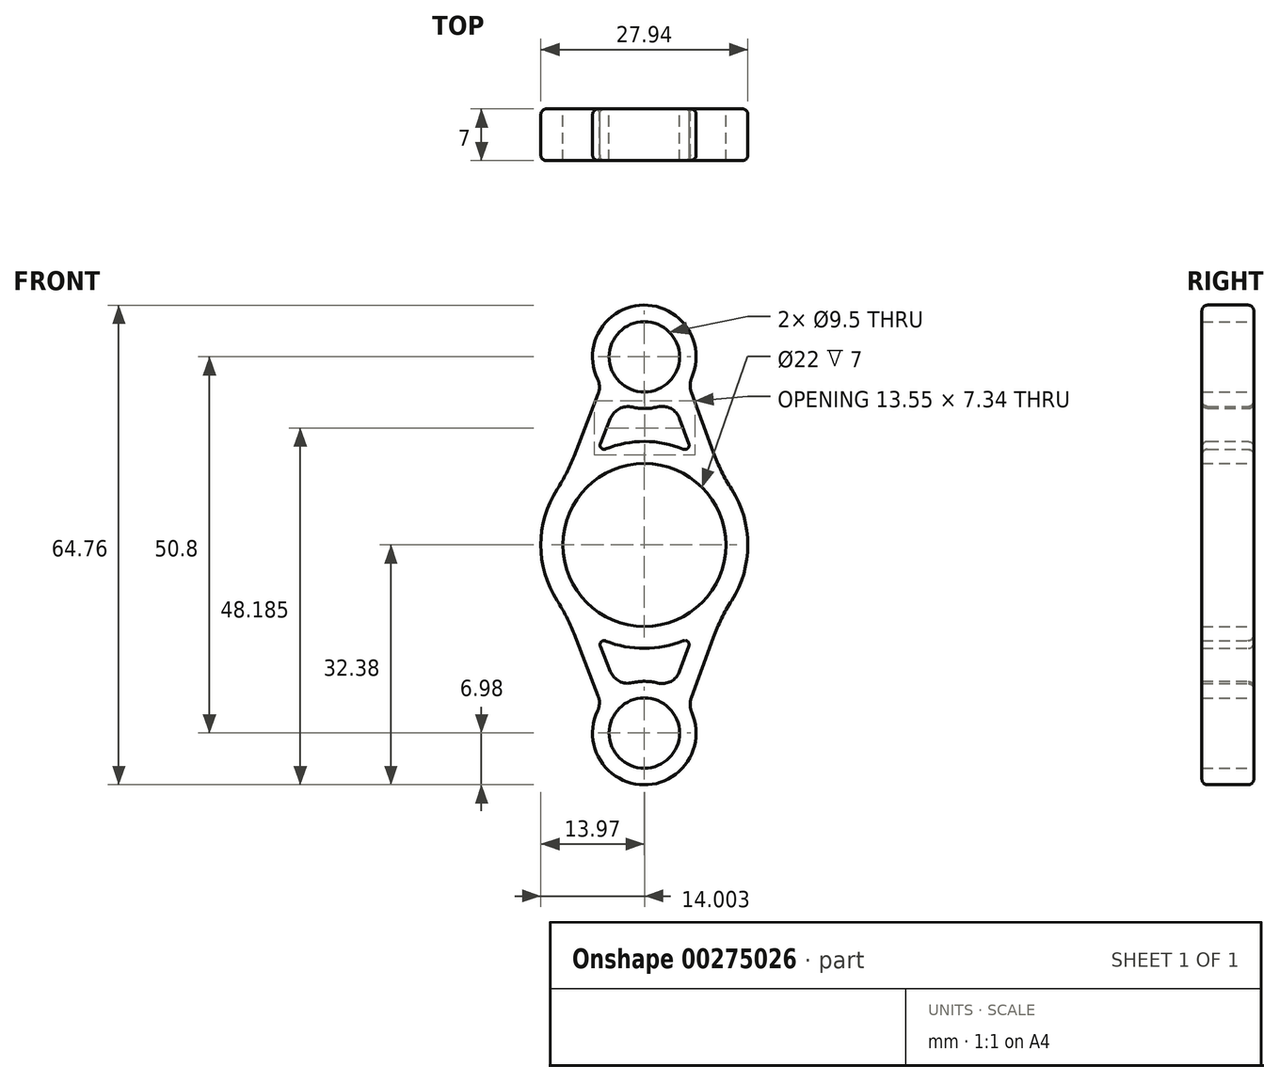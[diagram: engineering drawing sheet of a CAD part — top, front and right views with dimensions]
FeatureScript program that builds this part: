
annotation { "Feature Type Name" : "Feature", "Feature Type Description" : "" }
export const myFeature = defineFeature(function(context is Context, id is Id, definition is map)
    precondition{}
    {
        {
            var Q0;
            Q0=qCreatedBy(makeId("Front.planeOp"),FACE);
            var sketch = newSketch(context, id + "F0", { "sketchPlane" : qUnion([Q0])});
            skCircle(sketch, "E0", {"center": v(0, 0) * mm, "radius": 11 * mm});
            skArc(sketch, "E1", {"start": v(-11.77, 7.52) * mm, "mid": v(-13.97, 0) * mm, "end": v(-11.77, -7.52) * mm});
            skCircle(sketch, "E2", {"center": v(0, 0) * mm, "radius": 25.4 * mm, "construction": true});
            skCircle(sketch, "E3", {"center": v(0, 25.4) * mm, "radius": 4.75 * mm});
            skArc(sketch, "E4", {"start": v(6.4, 22.58) * mm, "mid": v(-0.1, 32.38) * mm, "end": v(-6.3, 22.4) * mm});
            skLineSegment(sketch, "E5", {"start": v(4.77, 17.05) * mm, "end": v(6.01, 13.64) * mm});
            skLineSegment(sketch, "E6.1", {"start": v(6.33, 20.7) * mm, "end": v(9.32, 12.49) * mm});
            skPoint(sketch, "E7.orphan", {"position": v(-11, 0) * mm});
            skArc(sketch, "E8.trimOffspring", {"start": v(5.28, 12.93) * mm, "mid": v(0.03, 13.97) * mm, "end": v(-5.22, 12.96) * mm});
            skPoint(sketch, "E9.trimOffspring.end.orphan", {"position": v(11, 0) * mm});
            skLineSegment(sketch, "E10.trimOffspring", {"start": v(-4.57, 17.09) * mm, "end": v(-5.94, 13.69) * mm});
            skLineSegment(sketch, "E11.trimOffspring", {"start": v(-6.23, 20.39) * mm, "end": v(-9.5, 11.98) * mm});
            skPoint(sketch, "E12.start.orphan", {"position": v(0, 30.15) * mm});
            skArc(sketch, "E13.trimOffspring", {"start": v(-1.62, 18.6) * mm, "mid": v(0.07, 18.42) * mm, "end": v(1.75, 18.64) * mm});
            skPoint(sketch, "E14.center.orphan", {"position": v(0, -25.4) * mm});
            skPoint(sketch, "E15.visualSharp", {"position": v(-5.8, 21.5) * mm});
            skArc(sketch, "E15.filletArc", {"start": v(-6.23, 20.39) * mm, "mid": v(-6.06, 21.4) * mm, "end": v(-6.3, 22.4) * mm});
            skPoint(sketch, "E16.visualSharp", {"position": v(5.95, 21.74) * mm});
            skArc(sketch, "E16.filletArc", {"start": v(6.4, 22.58) * mm, "mid": v(6.18, 21.64) * mm, "end": v(6.33, 20.7) * mm});
            skPoint(sketch, "E17.visualSharp", {"position": v(-3.62, 19.43) * mm});
            skArc(sketch, "E17.filletArc", {"start": v(-1.62, 18.6) * mm, "mid": v(-3.37, 18.4) * mm, "end": v(-4.57, 17.09) * mm});
            skPoint(sketch, "E18.visualSharp", {"position": v(3.85, 19.57) * mm});
            skArc(sketch, "E18.filletArc", {"start": v(4.77, 17.05) * mm, "mid": v(3.57, 18.43) * mm, "end": v(1.75, 18.64) * mm});
            skPoint(sketch, "E19.visualSharp", {"position": v(6.48, 12.38) * mm});
            skArc(sketch, "E19.filletArc", {"start": v(5.28, 12.93) * mm, "mid": v(5.88, 13.05) * mm, "end": v(6.01, 13.64) * mm});
            skPoint(sketch, "E20.visualSharp", {"position": v(-6.48, 12.38) * mm});
            skArc(sketch, "E20.filletArc", {"start": v(-5.94, 13.69) * mm, "mid": v(-5.82, 13.08) * mm, "end": v(-5.22, 12.96) * mm});
            skPoint(sketch, "E21.visualSharp", {"position": v(-10.65, 9.04) * mm});
            skArc(sketch, "E21.filletArc", {"start": v(-11.77, 7.52) * mm, "mid": v(-10.53, 9.7) * mm, "end": v(-9.5, 11.98) * mm});
            skPoint(sketch, "E22.visualSharp", {"position": v(10.52, 9.2) * mm});
            skArc(sketch, "E22.filletArc", {"start": v(9.32, 12.49) * mm, "mid": v(10.41, 9.94) * mm, "end": v(11.77, 7.52) * mm});
            skArc(sketch, "E23.MirrorCS", {"start": v(5.28, -12.93) * mm, "mid": v(5.88, -13.05) * mm, "end": v(6.01, -13.64) * mm});
            skArc(sketch, "E24.MirrorCS", {"start": v(-5.94, -13.69) * mm, "mid": v(-5.82, -13.08) * mm, "end": v(-5.22, -12.96) * mm});
            skArc(sketch, "E25.MirrorCS", {"start": v(-6.23, -20.39) * mm, "mid": v(-6.06, -21.4) * mm, "end": v(-6.3, -22.4) * mm});
            skArc(sketch, "E26.MirrorCS", {"start": v(6.4, -22.58) * mm, "mid": v(6.18, -21.64) * mm, "end": v(6.33, -20.7) * mm});
            skCircle(sketch, "E27.MirrorC", {"center": v(0, -25.4) * mm, "radius": 4.75 * mm});
            skLineSegment(sketch, "E28.MirrorCS", {"start": v(6.33, -20.7) * mm, "end": v(9.32, -12.49) * mm});
            skLineSegment(sketch, "E29.MirrorCS", {"start": v(4.77, -17.05) * mm, "end": v(6.01, -13.64) * mm});
            skPoint(sketch, "E30.MirrorP", {"position": v(-5.8, -21.5) * mm});
            skPoint(sketch, "E31.MirrorP", {"position": v(5.95, -21.74) * mm});
            skArc(sketch, "E32.MirrorCS", {"start": v(6.4, -22.58) * mm, "mid": v(-0.1, -32.38) * mm, "end": v(-6.3, -22.4) * mm});
            skArc(sketch, "E33.MirrorCS", {"start": v(5.28, -12.93) * mm, "mid": v(0.03, -13.97) * mm, "end": v(-5.22, -12.96) * mm});
            skArc(sketch, "E34.MirrorCS", {"start": v(-1.62, -18.6) * mm, "mid": v(0.07, -18.42) * mm, "end": v(1.75, -18.64) * mm});
            skPoint(sketch, "E35.MirrorP", {"position": v(-6.48, -12.38) * mm});
            skPoint(sketch, "E36.MirrorP", {"position": v(0, -30.15) * mm});
            skLineSegment(sketch, "E37.MirrorCS", {"start": v(-4.57, -17.09) * mm, "end": v(-5.94, -13.69) * mm});
            skLineSegment(sketch, "E38.MirrorCS", {"start": v(-6.23, -20.39) * mm, "end": v(-9.5, -11.98) * mm});
            skArc(sketch, "E39.MirrorCS", {"start": v(-11.77, -7.52) * mm, "mid": v(-10.53, -9.7) * mm, "end": v(-9.5, -11.98) * mm});
            skArc(sketch, "E40.MirrorCS", {"start": v(9.32, -12.49) * mm, "mid": v(10.41, -9.94) * mm, "end": v(11.77, -7.52) * mm});
            skPoint(sketch, "E41.MirrorP", {"position": v(3.85, -19.57) * mm});
            skArc(sketch, "E42.MirrorCS", {"start": v(-1.62, -18.6) * mm, "mid": v(-3.37, -18.4) * mm, "end": v(-4.57, -17.09) * mm});
            skArc(sketch, "E43.MirrorCS", {"start": v(4.77, -17.05) * mm, "mid": v(3.57, -18.43) * mm, "end": v(1.75, -18.64) * mm});
            skPoint(sketch, "E44.MirrorP", {"position": v(-10.65, -9.04) * mm});
            skPoint(sketch, "E45.MirrorP", {"position": v(6.48, -12.38) * mm});
            skPoint(sketch, "E46.MirrorP", {"position": v(-3.62, -19.43) * mm});
            skPoint(sketch, "E47.MirrorP", {"position": v(10.52, -9.2) * mm});
            skArc(sketch, "E48.trimOffspring", {"start": v(-5.22, -12.96) * mm, "mid": v(0.03, -13.97) * mm, "end": v(5.28, -12.93) * mm});
            skArc(sketch, "E49.trimOffspring", {"start": v(11.77, -7.52) * mm, "mid": v(13.97, 0) * mm, "end": v(11.77, 7.52) * mm});
            skSolve(sketch);
        }
        {
            var Q0;
            Q0 = qSketchRegion(id + "F0", true);
            extrude(context, id + "F1", {"entities" : qUnion([Q0]), "depth" : 7 * mm});
        }
        {
            var Q0;
            Q0=makeQuery(id+"F1.opExtrude","CAP_EDGE",EDGE,{"disambiguationData":[OSD([sQuery(id+"F0.wireOp",EDGE,"E21.filletArc")])],"isStart":false});
            var Q1;
            Q1=makeQuery(id+"F1.opExtrude","CAP_EDGE",EDGE,{"disambiguationData":[OSD([sQuery(id+"F0.wireOp",EDGE,"E8.trimOffspring")])],"isStart":false});
            var Q2;
            Q2=makeQuery(id+"F1.opExtrude","CAP_EDGE",EDGE,{"disambiguationData":[OSD([sQuery(id+"F0.wireOp",EDGE,"E48.trimOffspring")])],"isStart":false});
            var Q3;
            Q3=makeQuery(id+"F1.opExtrude","CAP_EDGE",EDGE,{"disambiguationData":[OSD([sQuery(id+"F0.wireOp",EDGE,"E49.trimOffspring")])],"isStart":true});
            var Q4;
            Q4=makeQuery(id+"F1.opExtrude","CAP_EDGE",EDGE,{"disambiguationData":[OSD([sQuery(id+"F0.wireOp",EDGE,"E5")])],"isStart":true});
            var Q5;
            Q5=makeQuery(id+"F1.opExtrude","CAP_EDGE",EDGE,{"disambiguationData":[OSD([sQuery(id+"F0.wireOp",EDGE,"E29.MirrorCS")])],"isStart":true});
            fillet(context, id + "F2", {"entities" : qUnion([Q0, Q1, Q2, Q3, Q4, Q5]), "radius" : 0.76 * mm, "tangentPropagation" : true, "allowEdgeOverflow" : false});
        }
    });
